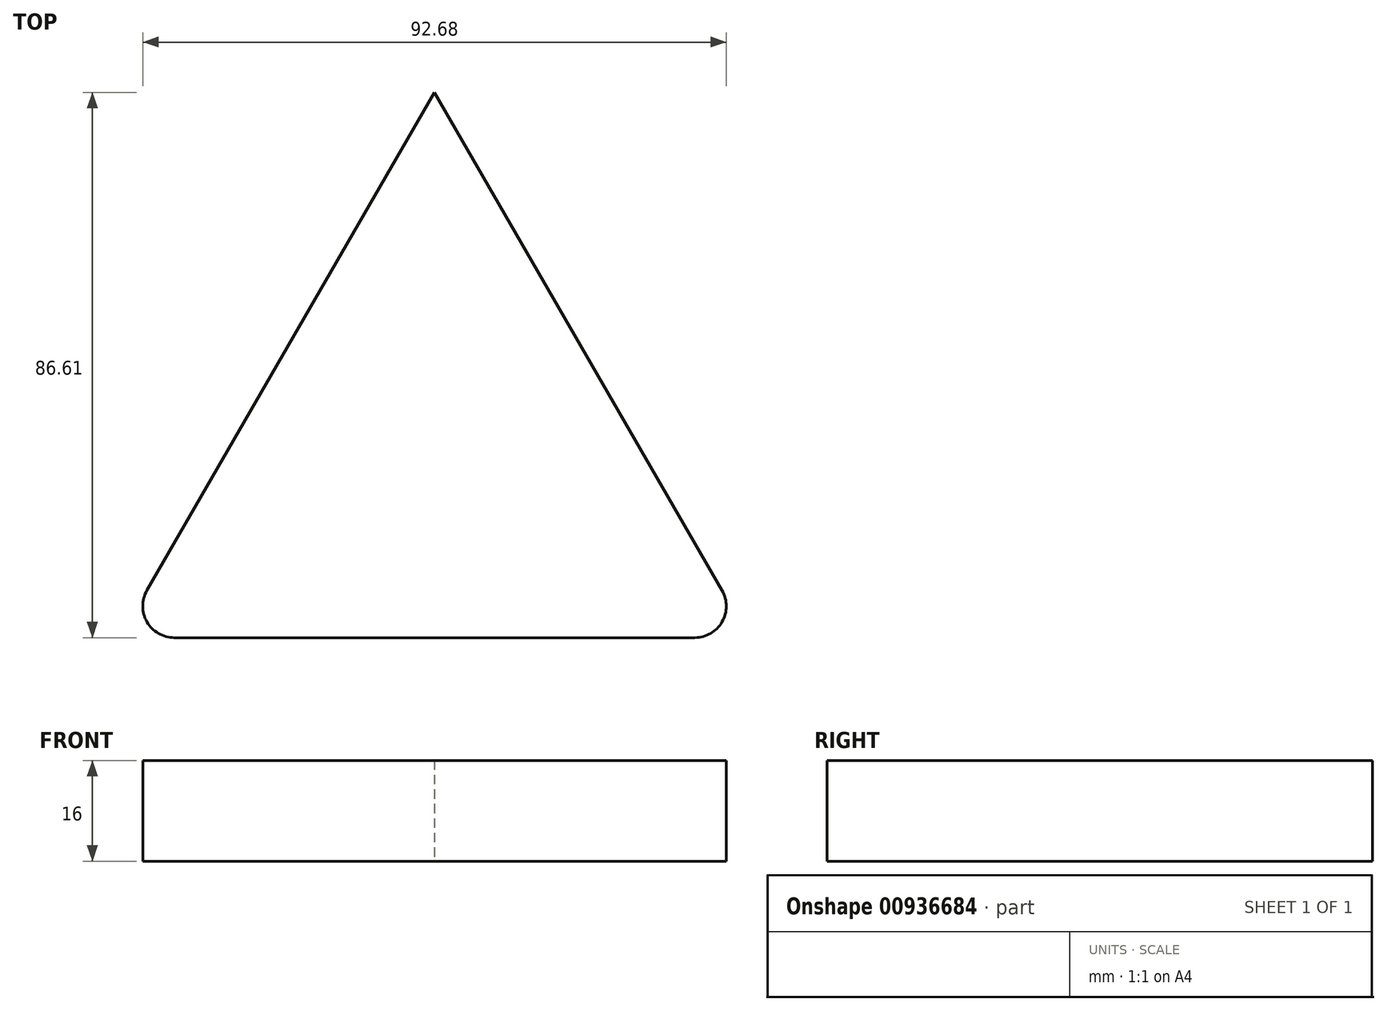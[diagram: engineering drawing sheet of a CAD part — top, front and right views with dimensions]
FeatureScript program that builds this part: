
annotation { "Feature Type Name" : "Feature", "Feature Type Description" : "" }
export const myFeature = defineFeature(function(context is Context, id is Id, definition is map)
    precondition{}
    {
        {
            var Q0;
            Q0=qCreatedBy(makeId("Top.planeOp"),FACE);
            var sketch = newSketch(context, id + "F0", { "sketchPlane" : qUnion([Q0])});
            skCircle(sketch, "E0.cCircle", {"center": v(0, 0) * mm, "radius": 28.87 * mm, "construction": true});
            skLineSegment(sketch, "E0.0", {"start": v(0, 57.74) * mm, "end": v(45.67, -21.37) * mm});
            skLineSegment(sketch, "E0.1", {"start": v(41.34, -28.87) * mm, "end": v(-41.34, -28.87) * mm});
            skLineSegment(sketch, "E0.2", {"start": v(-45.67, -21.37) * mm, "end": v(0, 57.74) * mm});
            skPoint(sketch, "E0.0.midPoint", {"position": v(25, 14.43) * mm});
            skLineSegment(sketch, "E1", {"start": v(0, 0) * mm, "end": v(63.06, 0) * mm});
            skPoint(sketch, "E2.visualSharp", {"position": v(-50, -28.87) * mm});
            skArc(sketch, "E2.filletArc", {"start": v(-45.67, -21.37) * mm, "mid": v(-45.67, -26.37) * mm, "end": v(-41.34, -28.87) * mm});
            skPoint(sketch, "E3.visualSharp", {"position": v(50, -28.87) * mm});
            skArc(sketch, "E3.filletArc", {"start": v(41.34, -28.87) * mm, "mid": v(45.67, -26.37) * mm, "end": v(45.67, -21.37) * mm});
            skSolve(sketch);
        }
        {
            var Q0;
            Q0=makeQuery(id+"F0.imprint","IMPRINT",FACE,{"disambiguationData":[TD([[makeQuery(id+"F0.imprint","IMPRINT",EDGE,{"derivedFrom":sQuery(id+"F0.wireOp",EDGE,"E0.1")}),-1.0]])]});
            extrude(context, id + "F1", {"entities" : qUnion([Q0]), "depth" : 16 * mm, "offsetDistance" : 25 * mm});
        }
    });
